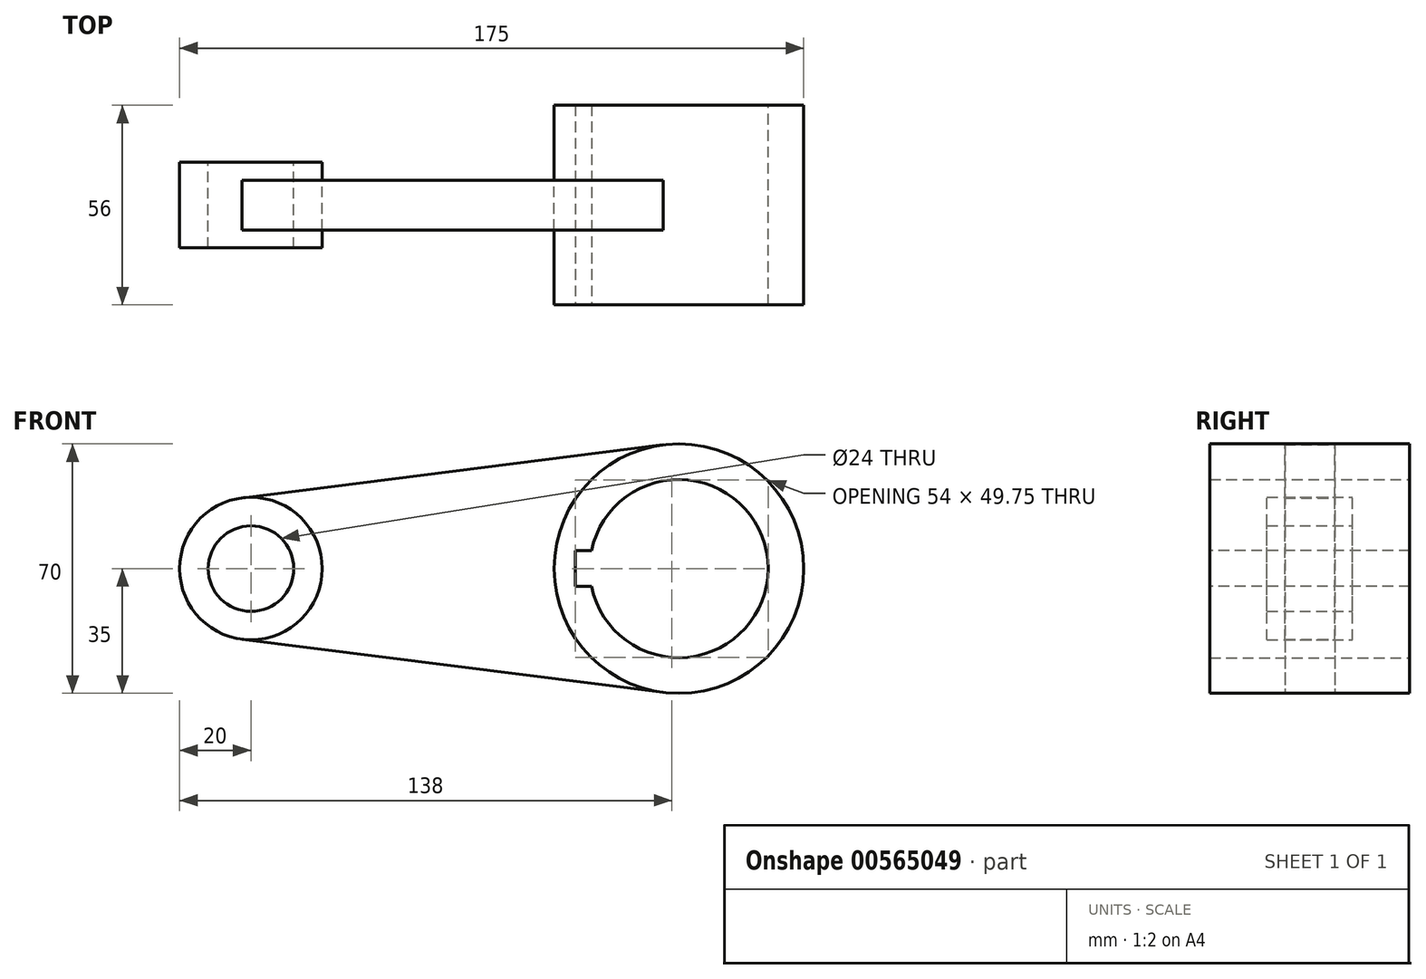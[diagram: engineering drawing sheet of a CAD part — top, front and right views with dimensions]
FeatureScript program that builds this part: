
annotation { "Feature Type Name" : "Feature", "Feature Type Description" : "" }
export const myFeature = defineFeature(function(context is Context, id is Id, definition is map)
    precondition{}
    {
        {
            var Q0;
            Q0=qCreatedBy(makeId("Front.planeOp"),FACE);
            var sketch = newSketch(context, id + "F0", { "sketchPlane" : qUnion([Q0])});
            skCircle(sketch, "E0", {"center": v(-51.74, 0) * mm, "radius": 12 * mm});
            skCircle(sketch, "E1", {"center": v(-51.74, 0) * mm, "radius": 20 * mm});
            skCircle(sketch, "E2", {"center": v(68.26, 0) * mm, "radius": 35 * mm});
            skCircle(sketch, "E3", {"center": v(68.26, 0) * mm, "radius": 25 * mm});
            skSolve(sketch);
        }
        {
            var Q0;
            Q0=makeQuery(id+"F0.imprint","IMPRINT",FACE,{"disambiguationData":[TD([[makeQuery(id+"F0.imprint","IMPRINT",EDGE,{"derivedFrom":sQuery(id+"F0.wireOp",EDGE,"E0")}),-1.0]])]});
            extrude(context, id + "F1", {"entities" : qUnion([Q0]), "depth" : 12 * mm, "offsetDistance" : 25 * mm, "hasSecondDirection" : true, "secondDirectionOppositeDirection" : true, "secondDirectionDepth" : 12 * mm});
        }
        {
            var Q0;
            Q0=makeQuery(id+"F0.imprint","IMPRINT",FACE,{"disambiguationData":[TD([[makeQuery(id+"F0.imprint","IMPRINT",EDGE,{"derivedFrom":sQuery(id+"F0.wireOp",EDGE,"E2")}),1.0]])]});
            extrude(context, id + "F2", {"entities" : qUnion([Q0]), "depth" : (56 / 2) * mm, "offsetDistance" : 25 * mm, "hasSecondDirection" : true, "secondDirectionOppositeDirection" : true, "secondDirectionDepth" : 28 * mm});
        }
        {
            var Q0;
            Q0=makeQuery(id+"F2.opExtrude","CAP_FACE",FACE,{"disambiguationData":[OSD([sQuery(id+"F0.wireOp",EDGE,"E2"),sQuery(id+"F0.wireOp",EDGE,"E3")])],"isStart":false});
            var sketch = newSketch(context, id + "F3", { "sketchPlane" : qUnion([Q0])});
            skLineSegment(sketch, "E4", {"start": v(43.26, 0) * mm, "end": v(39.26, 0) * mm});
            skLineSegment(sketch, "E5", {"start": v(39.26, 0) * mm, "end": v(39.26, 5) * mm});
            skLineSegment(sketch, "E6", {"start": v(39.26, 5) * mm, "end": v(47.57, 5) * mm});
            skLineSegment(sketch, "E7", {"start": v(39.26, 0) * mm, "end": v(39.26, -5) * mm});
            skLineSegment(sketch, "E8", {"start": v(39.26, -5) * mm, "end": v(48.95, -5) * mm});
            skSolve(sketch);
        }
        {
            var Q0;
            {var subQ0=sQuery(id+"F3.wireOp",EDGE,"E4");Q0=makeQuery(id+"F3.imprint","IMPRINT",FACE,{"disambiguationData":[TD([[makeQuery(id+"F3.imprint","IMPRINT",EDGE,{"derivedFrom":subQ0}),-1.0]])]});}
            var Q1;
            {var subQ0=sQuery(id+"F3.wireOp",EDGE,"E4");Q1=makeQuery(id+"F3.imprint","IMPRINT",FACE,{"disambiguationData":[TD([[makeQuery(id+"F3.imprint","IMPRINT",EDGE,{"derivedFrom":subQ0}),1.0]])]});}
            extrude(context, id + "F4", {"entities" : qUnion([Q0, Q1]), "operationType" : NewBodyOperationType.REMOVE, "oppositeDirection" : true, "depth" : 69.4 * mm, "offsetDistance" : 25 * mm});
        }
        {
            var Q0;
            Q0=qCreatedBy(makeId("Front.planeOp"),FACE);
            var sketch = newSketch(context, id + "F5", { "sketchPlane" : qUnion([Q0])});
            skLineSegment(sketch, "E9", {"start": v(-94.68, -14.75) * mm, "end": v(111.62, -40.74) * mm});
            skLineSegment(sketch, "E10", {"start": v(-84.8, 16) * mm, "end": v(80.49, 36.82) * mm});
            skCircle(sketch, "E11.0", {"center": v(-51.74, 0) * mm, "radius": 20 * mm});
            skCircle(sketch, "E12.0", {"center": v(68.26, 0) * mm, "radius": 35 * mm});
            skSolve(sketch);
        }
        {
            var Q0;
            {var subQ0=sQuery(id+"F5.wireOp",EDGE,"E11.0");var subQ1=sQuery(id+"F5.wireOp",EDGE,"E9");var subQ2=makeQuery(id+"F5.imprint","INTERSECT",VERTEX,{"derivedFrom":[subQ1,subQ0]});Q0=makeQuery(id+"F5.imprint","IMPRINT",FACE,{"disambiguationData":[TD([[makeQuery(id+"F5.imprint","IMPRINT",EDGE,{"disambiguationData":[TD([[subQ2,-1.0]])],"derivedFrom":subQ1}),1.0]])]});}
            extrude(context, id + "F6", {"entities" : qUnion([Q0]), "depth" : 7 * mm, "offsetDistance" : 25 * mm, "hasSecondDirection" : true, "secondDirectionOppositeDirection" : true, "secondDirectionDepth" : 7 * mm});
        }
    });
